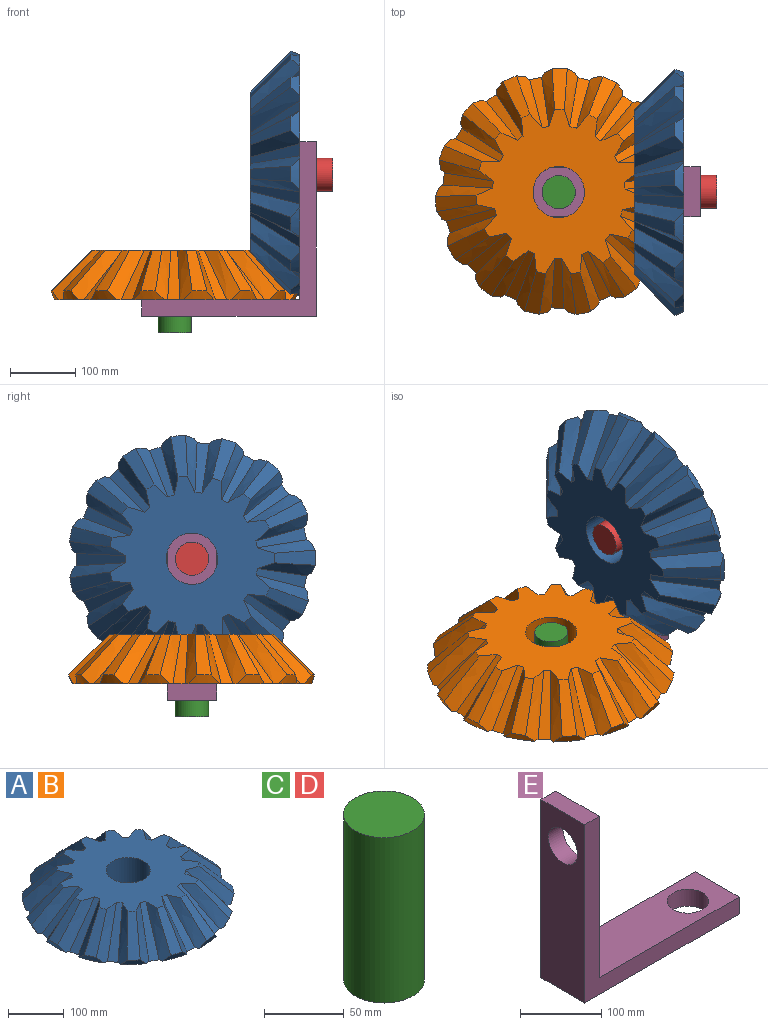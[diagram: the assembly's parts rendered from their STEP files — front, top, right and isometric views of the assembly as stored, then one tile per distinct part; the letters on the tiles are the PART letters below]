
ASSEMBLY  parts=5 mates=6
PART A: 78 faces, bbox 408.6x408.6x76.2 mm
  f0: plane 368.3x367.72mm, normal (0,0,-1), area 99421.2mm2, adj f2,f4,f6,f8,f10,f12,f14,f16
  f1: cone r=203.2mm half-angle=45deg, axis (0,0,-1), area 1668.1mm2, adj f2,f30,f33,f74
  f2: cone r=189.73mm half-angle=22.5deg, axis (0,0,1), area 520mm2, adj f0,f1,f33,f74
  f3: cone r=203.2mm half-angle=45deg, axis (0,0,-1), area 1668.1mm2, adj f4,f30,f71,f75
  f4: cone r=189.73mm half-angle=22.5deg, axis (0,0,1), area 520mm2, adj f0,f3,f71,f75
  f5: cone r=203.2mm half-angle=45deg, axis (0,0,-1), area 1668.1mm2, adj f6,f30,f68,f72
  f6: cone r=189.73mm half-angle=22.5deg, axis (0,0,1), area 520mm2, adj f0,f5,f68,f72
  f7: cone r=203.2mm half-angle=45deg, axis (0,0,-1), area 1668.1mm2, adj f8,f30,f65,f69
  f8: cone r=189.73mm half-angle=22.5deg, axis (0,0,1), area 520mm2, adj f0,f7,f65,f69
  f9: cone r=203.2mm half-angle=45deg, axis (0,0,-1), area 1668.1mm2, adj f10,f30,f62,f66
  f10: cone r=189.73mm half-angle=22.5deg, axis (0,0,1), area 520mm2, adj f0,f9,f62,f66
  f11: cone r=203.2mm half-angle=45deg, axis (0,0,-1), area 1668.1mm2, adj f12,f30,f59,f63
  f12: cone r=189.73mm half-angle=22.5deg, axis (0,0,1), area 520mm2, adj f0,f11,f59,f63
  f13: cone r=203.2mm half-angle=45deg, axis (0,0,-1), area 1668.1mm2, adj f14,f30,f56,f60
  f14: cone r=189.73mm half-angle=22.5deg, axis (0,0,1), area 520mm2, adj f0,f13,f56,f60
  f15: cone r=203.2mm half-angle=45deg, axis (0,0,-1), area 1668.1mm2, adj f16,f30,f53,f57
  f16: cone r=189.73mm half-angle=22.5deg, axis (0,0,1), area 520mm2, adj f0,f15,f53,f57
  f17: cone r=203.2mm half-angle=45deg, axis (0,0,-1), area 1668.1mm2, adj f18,f30,f50,f54
  f18: cone r=189.73mm half-angle=22.5deg, axis (0,0,1), area 520mm2, adj f0,f17,f50,f54
  f19: cone r=203.2mm half-angle=45deg, axis (0,0,-1), area 1668.1mm2, adj f20,f30,f47,f51
  f20: cone r=189.73mm half-angle=22.5deg, axis (0,0,1), area 520mm2, adj f0,f19,f47,f51
  f21: cone r=203.2mm half-angle=45deg, axis (0,0,-1), area 1668.1mm2, adj f22,f30,f44,f48
  f22: cone r=189.73mm half-angle=22.5deg, axis (0,0,1), area 520mm2, adj f0,f21,f44,f48
  f23: cone r=203.2mm half-angle=45deg, axis (0,0,-1), area 1668.1mm2, adj f24,f30,f41,f45
  f24: cone r=189.73mm half-angle=22.5deg, axis (0,0,1), area 520mm2, adj f0,f23,f41,f45
  f25: cone r=203.2mm half-angle=45deg, axis (0,0,-1), area 1668.1mm2, adj f26,f30,f38,f42
  f26: cone r=189.73mm half-angle=22.5deg, axis (0,0,1), area 520mm2, adj f0,f25,f38,f42
  f27: cone r=203.2mm half-angle=45deg, axis (0,0,-1), area 1668.1mm2, adj f28,f30,f35,f39
  f28: cone r=189.73mm half-angle=22.5deg, axis (0,0,1), area 520mm2, adj f0,f27,f35,f39
  f29: cone r=203.2mm half-angle=45deg, axis (0,0,-1), area 1668.1mm2, adj f30,f31,f32,f36
  f30: plane 253.72x252.54mm, normal (0,0,1), area 36412.8mm2, adj f1,f3,f5,f7,f9,f11,f13,f15
  f31: cone r=189.73mm half-angle=22.5deg, axis (0,0,1), area 520mm2, adj f0,f29,f32,f36
  f32: bspline ~101.6x76.2mm, area 2318.6mm2, adj f0,f29,f30,f31,f34
  f33: bspline ~99.08x76.2mm, area 2314.1mm2, adj f0,f1,f2,f30,f34
  f34: plane 76.2x76.2mm, normal (0.71,0,0.71), area 1594.3mm2, adj f0,f30,f32,f33
  f35: bspline ~81.96x76.2mm, area 2318.6mm2, adj f0,f27,f28,f30,f37
  f36: bspline ~103.67x76.2mm, area 2314.1mm2, adj f0,f29,f30,f31,f37
  f37: plane 76.2x75.63mm, normal (0.65,-0.29,0.71), area 1594.3mm2, adj f0,f30,f35,f36
  f38: bspline ~93.36x76.2mm, area 2318.6mm2, adj f0,f25,f26,f30,f40
  f39: bspline ~87.82x76.2mm, area 2314.1mm2, adj f0,f27,f28,f30,f40
  f40: plane 76.2x66.53mm, normal (0.47,-0.53,0.71), area 1594.3mm2, adj f0,f30,f38,f39
  f41: bspline ~104.88x76.2mm, area 2318.6mm2, adj f0,f23,f24,f30,f43
  f42: bspline ~86.68x76.2mm, area 2314.1mm2, adj f0,f25,f26,f30,f43
  f43: plane 77.04x76.2mm, normal (0.22,-0.67,0.71), area 1594.3mm2, adj f0,f30,f41,f42
  f44: bspline ~98.25x76.2mm, area 2318.6mm2, adj f0,f21,f22,f30,f46
  f45: bspline ~103.83x76.2mm, area 2314.1mm2, adj f0,f23,f24,f30,f46
  f46: plane 77.33x76.2mm, normal (-0.07,-0.7,0.71), area 1594.3mm2, adj f0,f30,f44,f45
  f47: bspline ~76.2x74.64mm, area 2318.6mm2, adj f0,f19,f20,f30,f49
  f48: bspline ~101.33x76.2mm, area 2314.1mm2, adj f0,f21,f22,f30,f49
  f49: plane 76.2x73.39mm, normal (-0.35,-0.61,0.71), area 1594.3mm2, adj f0,f30,f47,f48
  f50: bspline ~97.89x76.2mm, area 2318.6mm2, adj f0,f17,f18,f30,f52
  f51: bspline ~81.31x76.2mm, area 2314.1mm2, adj f0,f19,f20,f30,f52
  f52: plane 76.2x70.34mm, normal (-0.57,-0.42,0.71), area 1594.3mm2, adj f0,f30,f50,f51
  f53: bspline ~104.93x76.2mm, area 2318.6mm2, adj f0,f15,f16,f30,f55
  f54: bspline ~93.83x76.2mm, area 2314.1mm2, adj f0,f17,f18,f30,f55
  f55: plane 77.61x76.2mm, normal (-0.69,-0.15,0.71), area 1594.3mm2, adj f0,f30,f53,f54
  f56: bspline ~93.83x76.2mm, area 2318.6mm2, adj f0,f13,f14,f30,f58
  f57: bspline ~104.93x76.2mm, area 2314.1mm2, adj f0,f15,f16,f30,f58
  f58: plane 77.61x76.2mm, normal (-0.69,0.15,0.71), area 1594.3mm2, adj f0,f30,f56,f57
  f59: bspline ~81.31x76.2mm, area 2318.6mm2, adj f0,f11,f12,f30,f61
  f60: bspline ~97.89x76.2mm, area 2314.1mm2, adj f0,f13,f14,f30,f61
  f61: plane 76.2x70.34mm, normal (-0.57,0.42,0.71), area 1594.3mm2, adj f0,f30,f59,f60
  f62: bspline ~98.03x76.2mm, area 2318.6mm2, adj f0,f9,f10,f30,f64
  f63: bspline ~76.2x74.64mm, area 2314.1mm2, adj f0,f11,f12,f30,f64
  f64: plane 76.2x73.39mm, normal (-0.35,0.61,0.71), area 1594.3mm2, adj f0,f30,f62,f63
  f65: bspline ~101.1x76.2mm, area 2318.6mm2, adj f0,f7,f8,f30,f67
  f66: bspline ~98.25x76.2mm, area 2314.1mm2, adj f0,f9,f10,f30,f67
  f67: plane 77.33x76.2mm, normal (-0.07,0.7,0.71), area 1594.3mm2, adj f0,f30,f65,f66
  f68: bspline ~86.68x76.2mm, area 2318.6mm2, adj f0,f5,f6,f30,f70
  f69: bspline ~104.88x76.2mm, area 2314.1mm2, adj f0,f7,f8,f30,f70
  f70: plane 77.04x76.2mm, normal (0.22,0.67,0.71), area 1594.3mm2, adj f0,f30,f68,f69
  f71: bspline ~87.82x76.2mm, area 2318.6mm2, adj f0,f3,f4,f30,f73
  f72: bspline ~93.36x76.2mm, area 2314.1mm2, adj f0,f5,f6,f30,f73
  f73: plane 76.2x66.53mm, normal (0.47,0.53,0.71), area 1594.3mm2, adj f0,f30,f71,f72
  f74: bspline ~103.67x76.2mm, area 2318.6mm2, adj f0,f1,f2,f30,f76
  f75: bspline ~81.96x76.2mm, area 2314.1mm2, adj f0,f3,f4,f30,f76
  f76: plane 76.2x75.63mm, normal (0.65,0.29,0.71), area 1594.3mm2, adj f0,f30,f74,f75
  f77: cylinder r=39.37mm len=78.74mm, axis (0,0,1), area 18849.5mm2, adj f0,f30
PART B: same geometry as A
PART C: 3 faces, bbox 50.8x50.8x127 mm
  f0: cylinder r=25.4mm len=127mm, axis (0,0,-1), area 20268.3mm2, adj f1,f2
  f1: plane 50.8x50.8mm, normal (0,0,1), area 2026.8mm2, adj f0
  f2: plane 50.8x50.8mm, normal (0,0,-1), area 2026.8mm2, adj f0
PART D: same geometry as C
PART E: 10 faces, bbox 268x76.2x268 mm
  f0: plane 76.2x25.4mm, normal (0,0,1), area 1935.5mm2, adj f1,f5,f6,f7
  f1: plane 267.97x76.2mm, normal (-1,0,0), area 18392.5mm2, adj f0,f2,f6,f7,f9
  f2: plane 267.97x76.2mm, normal (0,0,-1), area 18392.5mm2, adj f1,f3,f6,f7,f8
  f3: plane 76.2x25.4mm, normal (1,0,0), area 1935.5mm2, adj f2,f4,f6,f7
  f4: plane 242.57x76.2mm, normal (0,0,1), area 16457mm2, adj f3,f5,f6,f7,f8
  f5: plane 242.57x76.2mm, normal (1,0,0), area 16457mm2, adj f0,f4,f6,f7,f9
  f6: plane 267.97x267.97mm, normal (0,-1,0), area 12967.7mm2, adj f0,f1,f2,f3,f4,f5
  f7: plane 267.97x267.97mm, normal (0,1,0), area 12967.7mm2, adj f0,f1,f2,f3,f4,f5
  f8: cylinder r=25.4mm len=50.8mm, axis (0,0,1), area 4053.7mm2, adj f2,f4
  f9: cylinder r=25.4mm len=50.8mm, axis (1,0,0), area 4053.7mm2, adj f1,f5
PLACE A rot(axis=(0.71,-0.04,-0.71),175.4deg) t=(191.77,0,217.17)mm
PLACE B rot(axis=(0,0,1),173.5deg) t=(0,0,25.4)mm
PLACE C rot(axis=(0,0,-1),96.5deg) t=(0,0,-25.4)mm
PLACE D rot(axis=(0.55,-0.62,-0.55),116.3deg) t=(242.57,0,217.17)mm
PLACE E rot(axis=(0,0,1),180deg) t=(217.17,0,0)mm
MATE cylindrical E.f8 <-> C.f0  axis (0,0,1) through (0,0,12.7)mm
MATE fastened C.f0 <-> B.f77  axis (0,0,1) through (0,0,101.6)mm
MATE revolute B.f77 <-> E.f8  axis (0,0,-1) through (0,0,25.4)mm
MATE revolute A.f1 <-> E.f9  axis (1,0,0) through (191.77,0,217.17)mm
MATE fastened D.f0 <-> A.f77  axis (-1,0,0) through (115.57,0,217.17)mm
MATE cylindrical E.f9 <-> D.f0  axis (-1,0,0) through (204.47,0,217.17)mm
